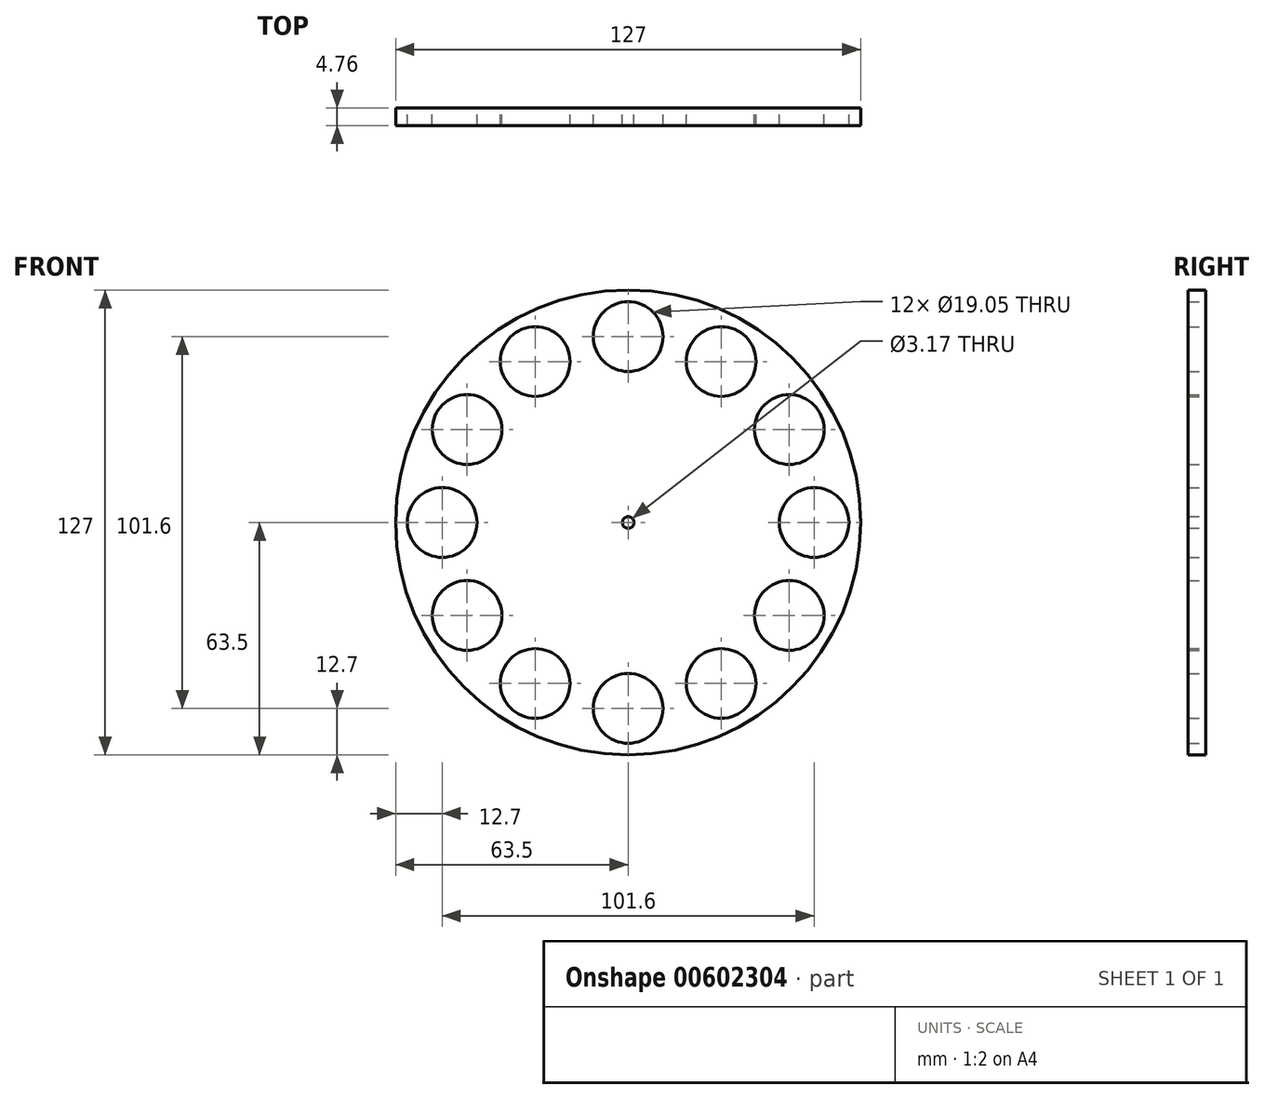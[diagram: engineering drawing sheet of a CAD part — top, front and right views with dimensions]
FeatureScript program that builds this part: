
annotation { "Feature Type Name" : "Feature", "Feature Type Description" : "" }
export const myFeature = defineFeature(function(context is Context, id is Id, definition is map)
    precondition{}
    {
        {
            var Q0;
            Q0=qCreatedBy(makeId("Front.planeOp"),FACE);
            var sketch = newSketch(context, id + "F0", { "sketchPlane" : qUnion([Q0])});
            skCircle(sketch, "E0", {"center": v(0, 0) * mm, "radius": 63.5 * mm});
            skCircle(sketch, "E1", {"center": v(0, 50.8) * mm, "radius": 9.53 * mm});
            skCircle(sketch, "E2", {"center": v(0, 0) * mm, "radius": 50.8 * mm, "construction": true});
            skCircle(sketch, "E3.1.0", {"center": v(-25.4, 44) * mm, "radius": 9.53 * mm});
            skCircle(sketch, "E3.2.0", {"center": v(-44, 25.4) * mm, "radius": 9.53 * mm});
            skCircle(sketch, "E3.3.0", {"center": v(-50.8, 0) * mm, "radius": 9.53 * mm});
            skCircle(sketch, "E3.4.0", {"center": v(-44, -25.4) * mm, "radius": 9.53 * mm});
            skCircle(sketch, "E3.5.0", {"center": v(-25.4, -44) * mm, "radius": 9.53 * mm});
            skCircle(sketch, "E3.6.0", {"center": v(0, -50.8) * mm, "radius": 9.52 * mm});
            skCircle(sketch, "E3.7.0", {"center": v(25.4, -44) * mm, "radius": 9.53 * mm});
            skCircle(sketch, "E3.8.0", {"center": v(44, -25.4) * mm, "radius": 9.53 * mm});
            skCircle(sketch, "E3.9.0", {"center": v(50.8, 0) * mm, "radius": 9.53 * mm});
            skCircle(sketch, "E4", {"center": v(0, 0) * mm, "radius": 1.59 * mm});
            skCircle(sketch, "E5.1.10.0", {"center": v(44, 25.4) * mm, "radius": 9.53 * mm});
            skCircle(sketch, "E5.1.11.0", {"center": v(25.4, 44) * mm, "radius": 9.53 * mm});
            skSolve(sketch);
        }
        {
            var Q0;
            Q0=qSketchRegion(id+"F0",true);
            extrude(context, id + "F1", {"entities" : qUnion([Q0]), "depth" : 4.76 * mm, "offsetDistance" : 25.4 * mm});
        }
    });
